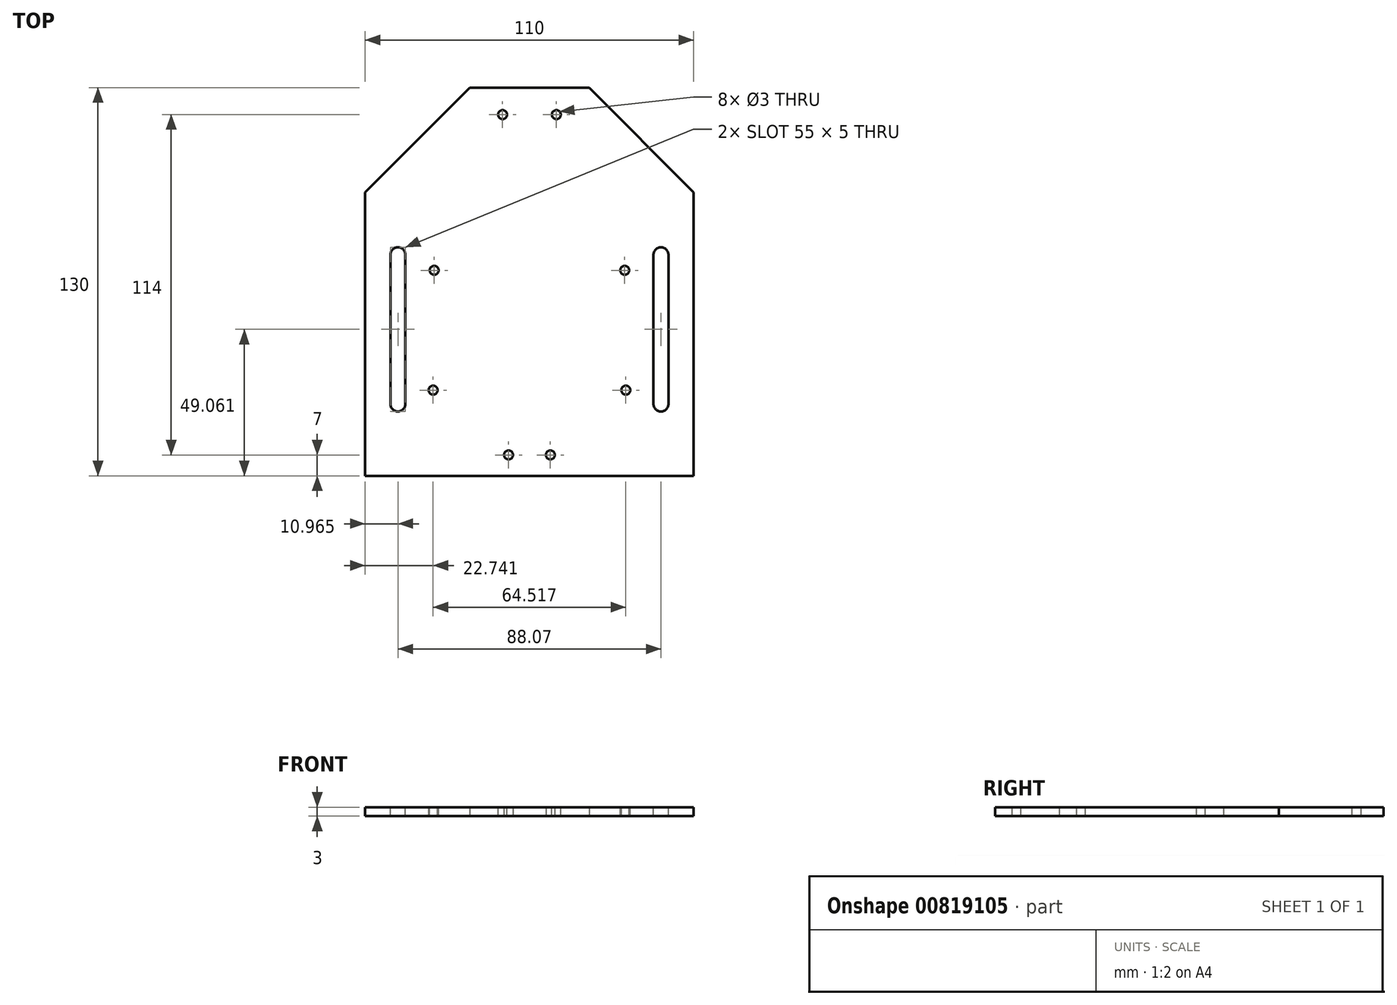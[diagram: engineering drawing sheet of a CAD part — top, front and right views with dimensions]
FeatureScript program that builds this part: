
annotation { "Feature Type Name" : "Feature", "Feature Type Description" : "" }
export const myFeature = defineFeature(function(context is Context, id is Id, definition is map)
    precondition{}
    {
        {
            var Q0;
            Q0=qCreatedBy(makeId("Top.planeOp"),FACE);
            var sketch = newSketch(context, id + "F0", { "sketchPlane" : qUnion([Q0])});
            skLineSegment(sketch, "E0.bottom", {"start": v(0, 0) * mm, "end": v(55, 0) * mm});
            skLineSegment(sketch, "E0.top", {"start": v(0, 130) * mm, "end": v(55, 130) * mm});
            skLineSegment(sketch, "E0.left", {"start": v(0, 0) * mm, "end": v(0, 130) * mm});
            skLineSegment(sketch, "E0.right", {"start": v(55, 0) * mm, "end": v(55, 130) * mm});
            skSolve(sketch);
        }
        {
            var Q0;
            Q0=makeQuery(id+"F0.imprint","IMPRINT",FACE,{"disambiguationData":[TD([[makeQuery(id+"F0.imprint","IMPRINT",EDGE,{"derivedFrom":sQuery(id+"F0.wireOp",EDGE,"E0.bottom")}),1.0]])]});
            extrude(context, id + "F1", {"entities" : qUnion([Q0]), "depth" : 3 * mm, "offsetDistance" : 25 * mm});
        }
        {
            var Q0;
            Q0=makeQuery(id+"F1.opExtrude","SWEPT_EDGE",EDGE,{"disambiguationData":[OSD([sQuery(id+"F0.wireOp",EDGE,"E0.top"),sQuery(id+"F0.wireOp",EDGE,"E0.right")])]});
            chamfer(context, id + "F2", {"entities" : qUnion([Q0]), "width" : 35 * mm, "tangentPropagation" : true});
        }
        {
            var Q0;
            {var subQ0=makeQuery(id+"F1.opExtrude","CAP_FACE",FACE,{"disambiguationData":[OSD([sQuery(id+"F0.wireOp",EDGE,"E0.bottom"),sQuery(id+"F0.wireOp",EDGE,"E0.top"),sQuery(id+"F0.wireOp",EDGE,"E0.left"),sQuery(id+"F0.wireOp",EDGE,"E0.right")])],"isStart":false});Q0=makeQuery(id+"F1OklB9v31usyYk_1.boolean.opBoolean","MERGE",FACE,{"derivedFrom":[subQ0,makeQuery(id+"F1OklB9v31usyYk_1.opPattern","COPY",FACE,{"derivedFrom":subQ0,"instanceName":"1"})]});}
            var sketch = newSketch(context, id + "F3", { "sketchPlane" : qUnion([Q0])});
            skLineSegment(sketch, "E1", {"start": v(44.03, 74.06) * mm, "end": v(44.03, 24.06) * mm});
            skArc(sketch, "E2.0.startCap", {"start": v(41.53, 74.06) * mm, "mid": v(44.03, 76.56) * mm, "end": v(46.53, 74.06) * mm});
            skArc(sketch, "E2.0.endCap", {"start": v(46.53, 24.06) * mm, "mid": v(44.03, 21.56) * mm, "end": v(41.53, 24.06) * mm});
            skLineSegment(sketch, "E2.0.left", {"start": v(46.53, 74.06) * mm, "end": v(46.53, 24.06) * mm});
            skLineSegment(sketch, "E2.0.right", {"start": v(41.53, 74.06) * mm, "end": v(41.53, 24.06) * mm});
            skSolve(sketch);
        }
        {
            var Q0;
            Q0 = qSketchRegion(id + "F3", true);
            extrude(context, id + "F4", {"entities" : qUnion([Q0]), "operationType" : NewBodyOperationType.REMOVE, "oppositeDirection" : true, "depth" : 34.03 * mm, "offsetDistance" : 25 * mm});
        }
        {
            var Q0;
            Q0=makeQuery(id+"F1.opExtrude","CAP_FACE",FACE,{"disambiguationData":[OSD([sQuery(id+"F0.wireOp",EDGE,"E0.bottom"),sQuery(id+"F0.wireOp",EDGE,"E0.top"),sQuery(id+"F0.wireOp",EDGE,"E0.left"),sQuery(id+"F0.wireOp",EDGE,"E0.right")])],"isStart":false});
            var sketch = newSketch(context, id + "F5", { "sketchPlane" : qUnion([Q0])});
            skLineSegment(sketch, "E3", {"start": v(31.9, 68.84) * mm, "end": v(31.9, 30.93) * mm});
            skLineSegment(sketch, "E4", {"start": v(31.9, 30.93) * mm, "end": v(31.9, 68.84) * mm});
            skSolve(sketch);
        }
        {
            var Q0;
            Q0=sQuery(id+"F5.wireOp",VERTEX,"E3.start");
            var Q1;
            Q1=makeQuery(id+"F1.opExtrude","SWEPT_BODY",BODY,{"disambiguationData":[OSD([sQuery(id+"F0.wireOp",EDGE,"E0.bottom"),sQuery(id+"F0.wireOp",EDGE,"E0.top"),sQuery(id+"F0.wireOp",EDGE,"E0.left"),sQuery(id+"F0.wireOp",EDGE,"E0.right")])]});
            hole(context, id + "F6", {"style" : HoleStyle.SIMPLE, "endStyle" : HoleEndStyle.THROUGH, "holeDiameter" : 3 * mm, "majorDiameter" : 5 * mm, "isTappedThrough" : true, "tappedDepth" : 12 * mm, "tapClearance" : 3, "locations" : qUnion([Q0]), "scope" : qUnion([Q1])});
        }
        {
            var Q0;
            Q0=makeQuery(id+"F1.opExtrude","CAP_FACE",FACE,{"disambiguationData":[OSD([sQuery(id+"F0.wireOp",EDGE,"E0.bottom"),sQuery(id+"F0.wireOp",EDGE,"E0.top"),sQuery(id+"F0.wireOp",EDGE,"E0.left"),sQuery(id+"F0.wireOp",EDGE,"E0.right")])],"isStart":false});
            var sketch = newSketch(context, id + "F7", { "sketchPlane" : qUnion([Q0])});
            skLineSegment(sketch, "E5", {"start": v(32.26, 28.7) * mm, "end": v(32.26, 67.38) * mm});
            skSolve(sketch);
        }
        {
            var Q0;
            Q0=sQuery(id+"F7.wireOp",VERTEX,"E5.start");
            var Q1;
            Q1=makeQuery(id+"F1.opExtrude","SWEPT_BODY",BODY,{"disambiguationData":[OSD([sQuery(id+"F0.wireOp",EDGE,"E0.bottom"),sQuery(id+"F0.wireOp",EDGE,"E0.top"),sQuery(id+"F0.wireOp",EDGE,"E0.left"),sQuery(id+"F0.wireOp",EDGE,"E0.right")])]});
            hole(context, id + "F8", {"style" : HoleStyle.SIMPLE, "endStyle" : HoleEndStyle.THROUGH, "holeDiameter" : 3 * mm, "majorDiameter" : 5 * mm, "isTappedThrough" : true, "tappedDepth" : 12 * mm, "tapClearance" : 3, "locations" : qUnion([Q0]), "scope" : qUnion([Q1])});
        }
        {
            var Q0;
            Q0=makeQuery(id+"F1.opExtrude","CAP_FACE",FACE,{"disambiguationData":[OSD([sQuery(id+"F0.wireOp",EDGE,"E0.bottom"),sQuery(id+"F0.wireOp",EDGE,"E0.top"),sQuery(id+"F0.wireOp",EDGE,"E0.left"),sQuery(id+"F0.wireOp",EDGE,"E0.right")])],"isStart":true});
            var sketch = newSketch(context, id + "F9", { "sketchPlane" : qUnion([Q0])});
            skCircle(sketch, "E6", {"center": v(7, -7) * mm, "radius": 1.5 * mm});
            skSolve(sketch);
        }
        {
            var Q0;
            Q0 = qSketchRegion(id + "F9", true);
            extrude(context, id + "F10", {"entities" : qUnion([Q0]), "operationType" : NewBodyOperationType.REMOVE, "oppositeDirection" : true, "depth" : 25 * mm, "offsetDistance" : 25 * mm});
        }
        {
            var Q0;
            Q0=makeQuery(id+"F1.opExtrude","CAP_FACE",FACE,{"disambiguationData":[OSD([sQuery(id+"F0.wireOp",EDGE,"E0.bottom"),sQuery(id+"F0.wireOp",EDGE,"E0.top"),sQuery(id+"F0.wireOp",EDGE,"E0.left"),sQuery(id+"F0.wireOp",EDGE,"E0.right")])],"isStart":false});
            var sketch = newSketch(context, id + "F11", { "sketchPlane" : qUnion([Q0])});
            skCircle(sketch, "E7", {"center": v(9, 121) * mm, "radius": 1.5 * mm});
            skSolve(sketch);
        }
        {
            var Q0;
            Q0 = qSketchRegion(id + "F11", true);
            extrude(context, id + "F12", {"entities" : qUnion([Q0]), "operationType" : NewBodyOperationType.REMOVE, "oppositeDirection" : true, "depth" : 25 * mm, "offsetDistance" : 25 * mm});
        }
        {
            var Q0;
            Q0=makeQuery(id+"F1.opExtrude","CAP_FACE",FACE,{"disambiguationData":[OSD([sQuery(id+"F0.wireOp",EDGE,"E0.bottom"),sQuery(id+"F0.wireOp",EDGE,"E0.top"),sQuery(id+"F0.wireOp",EDGE,"E0.left"),sQuery(id+"F0.wireOp",EDGE,"E0.right")])],"isStart":false});
            var sketch = newSketch(context, id + "F13", { "sketchPlane" : qUnion([Q0])});
            skSolve(sketch);
        }
        {
            var Q0;
            Q0=makeQuery(id+"F1.opExtrude","SWEPT_BODY",BODY,{"disambiguationData":[OSD([sQuery(id+"F0.wireOp",EDGE,"E0.bottom"),sQuery(id+"F0.wireOp",EDGE,"E0.top"),sQuery(id+"F0.wireOp",EDGE,"E0.left"),sQuery(id+"F0.wireOp",EDGE,"E0.right")])]});
            var Q1;
            Q1=qCreatedBy(makeId("Right.planeOp"),FACE);
            mirror(context, id + "F14", {"operationType" : NewBodyOperationType.ADD, "entities" : qUnion([Q0]), "mirrorPlane" : qUnion([Q1])});
        }
    });
